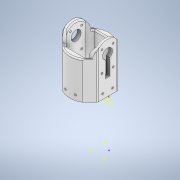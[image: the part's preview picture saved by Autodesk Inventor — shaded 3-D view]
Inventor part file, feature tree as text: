
AUTODESK INVENTOR PART (.ipt)
format: ipt  version: 2021 (Build 250183000, 183)  size: 475,136 bytes
history: native  units: mm
features: sketch x20, extrude x17, fillet x3, other x1
ambient origin geometry x8: Origin, YZ Plane, XZ Plane, XY Plane, X Axis, Y Axis, Z Axis, Center Point
bodies: Body1 (feature_tree)
feature tree (41):
  other  "Sólido1"
  extrude  "Extrusión1"  Depth=40.0mm TaperAngle=360.0deg
  extrude  "Extrusión4"  Depth=2.0mm
  extrude  "Extrusión5"  Depth=70.0mm TaperAngle=0.0deg
  extrude  "Extrusión6"  Depth=3.0mm
  extrude  "Extrusión7"  Depth=700.0mm TaperAngle=0.0deg
  extrude  "Extrusión8"  Depth=3.0mm
  extrude  "Extrusión9"  Depth=700.0mm TaperAngle=0.0deg
  fillet  "Empalme3"  Radius=2.0mm
  fillet  "Empalme4"  Radius=2.0mm
  sketch  "Boceto12"  dims[d82=700.0mm d83=0.0mm d84=700.0mm d85=0.0mm d86=2.0mm d87=2.0mm]
  sketch  "Boceto13"  dims[d88=60.0mm d89=0.0mm d95=600.0mm d96=0.0mm]
  sketch  "Boceto14"  dims[d103=600.0mm d104=0.0mm d115=16.0mm]
  extrude  "Extrusión10"  Depth=600.0mm TaperAngle=0.0deg
  extrude  "Extrusión11"  Depth=16.0mm
  extrude  "Extrusión12"  Depth=25.0mm
  extrude  "Extrusión13"  Depth=30.0mm TaperAngle=0.0deg
  extrude  "Extrusión14"  Depth=8.0mm
  sketch  "Boceto19"  dims[d138=3.0mm d139=300.0mm d140=0.0mm]
  extrude  "Extrusión15"  Depth=3.0mm
  extrude  "Extrusión16"  Depth=300.0mm TaperAngle=0.0deg
  extrude  "Extrusión17"  Depth=0.3mm
  sketch  "Boceto23"  dims[d150=3.0mm]
  extrude  "Extrusión18"  Depth=3.0mm
  extrude  "Extrusión19"  Depth=0.3mm
  fillet  "Empalme5"  Radius=3.0mm
  sketch  "Boceto1"  dims[d3=22.5mm d5=40.0mm d7=360.0deg]
  sketch  "Boceto6"  dims[d9=100.0mm d10=0.0mm d38=2.0mm]
  sketch  "Boceto8"  dims[d39=70.0mm d40=0.0mm d51=70.0mm d52=0.0mm]
  sketch  "Boceto9"  dims[d66=700.0mm d67=0.0mm d73=3.0mm]
  sketch  "Boceto10"  dims[d74=3.0mm d75=700.0mm d76=0.0mm]
  sketch  "Boceto11"  dims[d80=3.0mm d81=3.0mm]
  sketch  "Boceto15"  dims[d116=600.0mm d117=0.0mm d120=25.0mm]
  sketch  "Boceto16"  dims[d122=600.0mm d123=0.0mm d124=30.0mm d125=0.0mm]
  sketch  "Boceto17"  dims[d131=300.0mm d132=0.0mm d133=8.0mm]
  sketch  "Boceto18"  dims[d135=8.0mm d137=3.0mm]
  sketch  "Boceto20"  dims[d141=100.0mm d142=0.0mm d143=0.3mm]
  sketch  "Boceto21"  dims[d145=3.0mm d146=3.0mm]
  sketch  "Boceto22"  dims[d147=0.3mm d148=0.3mm d149=3.0mm]
  sketch  "Boceto24"  dims[d151=100.0mm d152=0.0mm]
  sketch  "Boceto25"  dims[d153=4.0mm d41=0.872665mm d53=0.5mm d54=0.872665mm d55=0.5mm d56=0.872665mm d90=0.5mm d91=0.872665mm]
